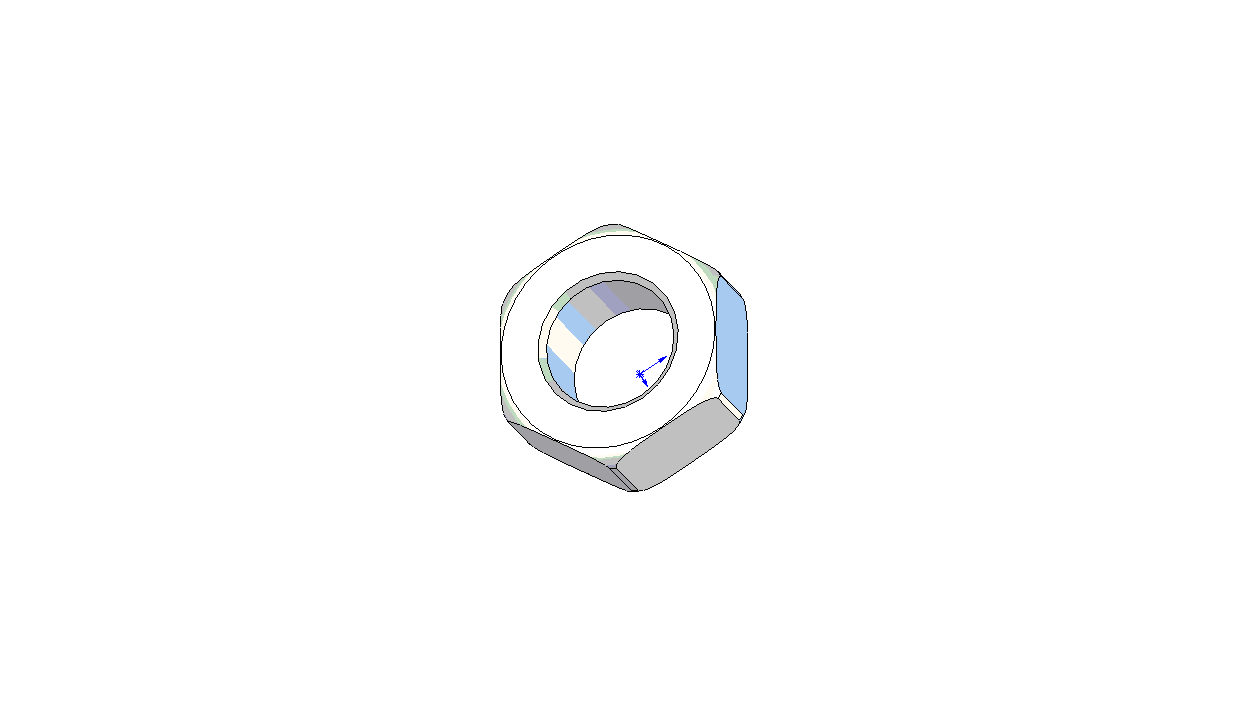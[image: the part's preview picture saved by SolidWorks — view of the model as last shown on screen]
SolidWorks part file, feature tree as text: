
SOLIDWORKS PART (.sldprt)
format: sldprt  version: not decoded by parser v0  size: 120,832 bytes
history: native  units: mm
features: plane x3, sketch x2, material x1, extrude x1, fillet x1, cut_extrude x1, chamfer x1 (+8 scaffold rows collapsed)
feature tree (18):
  scaffold x8  (default folders/planes/origin — collapsed)
  material  "Matériau <non spécifié>"
  plane  "Plan de face"
  plane  "Plan de dessus"
  plane  "Plan de droite"
  sketch  "Esquisse1"  dims[D1=~2.236275mm]
  extrude  "Extrusion1"  Depth=3mm
  fillet  "Congé1"  Radius=0.5mm
  sketch  "Esquisse2"  dims[c1.D1=7.8mm c2.D1=60.0deg c2.D2=~7.800825mm c3.D2=60.0deg]
  cut_extrude  "Enlèv. mat.-Extru.1"  Depth=3mm
  chamfer  "Chanfrein1"  Distance=0.2mm Angle=45deg
decode coverage: 6 of 6 modeling features carry decoded parameters
note: ~ marks probable driven/reference dimensions
note: suppression state not decoded; provenance and decode notes live in map.json
